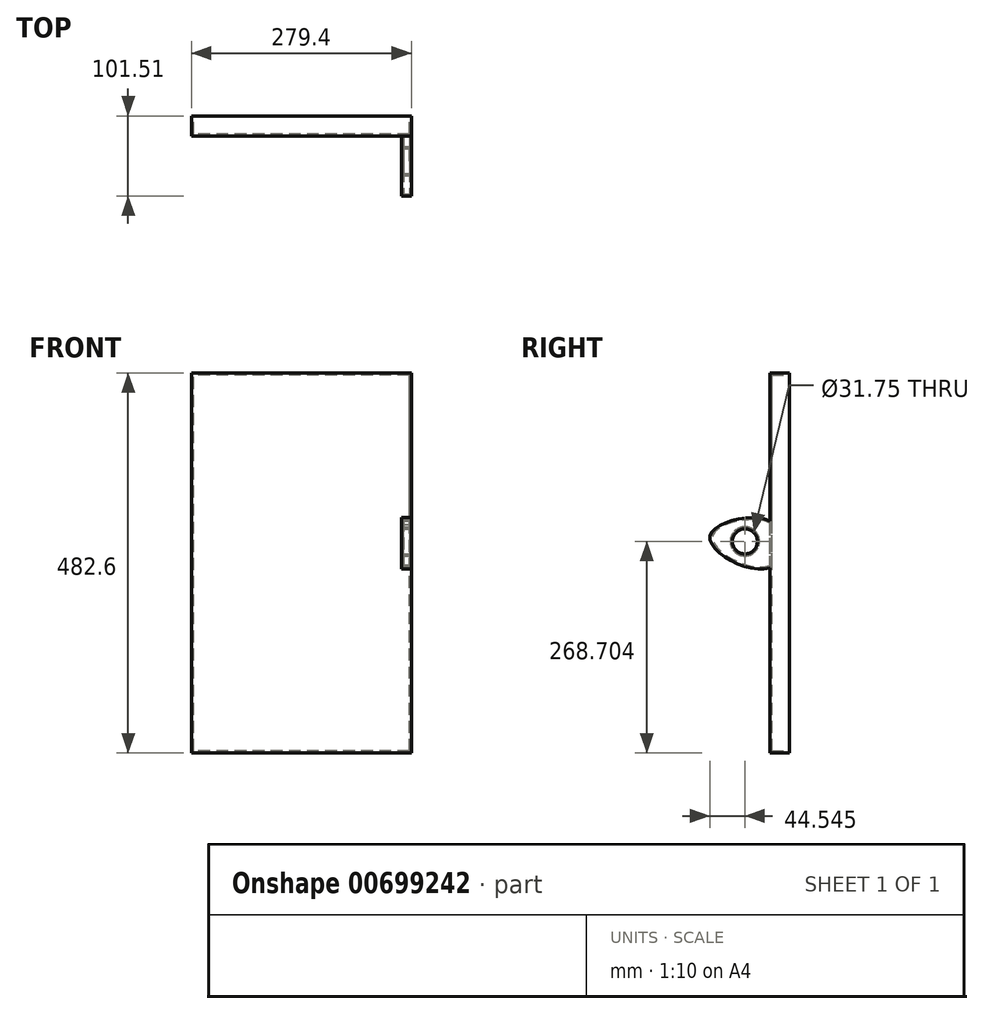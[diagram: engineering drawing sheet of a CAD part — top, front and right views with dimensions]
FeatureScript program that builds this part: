
annotation { "Feature Type Name" : "Feature", "Feature Type Description" : "" }
export const myFeature = defineFeature(function(context is Context, id is Id, definition is map)
    precondition{}
    {
        {
            var Q0;
            Q0=qCreatedBy(makeId("Front.planeOp"),FACE);
            var sketch = newSketch(context, id + "F0", { "sketchPlane" : qUnion([Q0])});
            skLineSegment(sketch, "E0.bottom", {"start": v(0, 0) * mm, "end": v(-279.4, 0) * mm});
            skLineSegment(sketch, "E0.top", {"start": v(0, 482.6) * mm, "end": v(-279.4, 482.6) * mm});
            skLineSegment(sketch, "E0.left", {"start": v(0, 0) * mm, "end": v(0, 482.6) * mm});
            skLineSegment(sketch, "E0.right", {"start": v(-279.4, 0) * mm, "end": v(-279.4, 482.6) * mm});
            skPoint(sketch, "E1.first.point", {"position": v(-64.83, 242.95) * mm});
            skPoint(sketch, "E1.second.point", {"position": v(-76.02, 242.95) * mm});
            skPoint(sketch, "E1.third.point", {"position": v(-52.5, 330.29) * mm});
            skSolve(sketch);
        }
        {
            var Q0;
            Q0=makeQuery(id+"F0.imprint","IMPRINT",FACE,{"disambiguationData":[TD([[makeQuery(id+"F0.imprint","IMPRINT",EDGE,{"derivedFrom":sQuery(id+"F0.wireOp",EDGE,"E0.bottom")}),-1.0]])]});
            extrude(context, id + "F1", {"entities" : qUnion([Q0]), "depth" : 25.4 * mm, "offsetDistance" : 25.4 * mm});
        }
        {
            var Q0;
            Q0=makeQuery(id+"F1.opExtrude","SWEPT_FACE",FACE,{"disambiguationData":[OSD([sQuery(id+"F0.wireOp",EDGE,"E0.left")])]});
            var sketch = newSketch(context, id + "F2", { "sketchPlane" : qUnion([Q0])});
            skPoint(sketch, "E2.0.internal.snap0", {"position": v(-25.4, 241.3) * mm});
            skPoint(sketch, "E2.4.internal.snap0", {"position": v(-25.4, 241.3) * mm});
            skFitSpline(sketch, "E2", {"points": [v(-15.12, 241.3) * mm, v(-14, 285.5) * mm, v(-61.03, 297.82) * mm, v(-101.34, 275.42) * mm, v(-68.86, 241.3) * mm, v(-15.12, 241.3) * mm]});
            skSolve(sketch);
        }
        {
            var Q0;
            {var subQ0=sQuery(id+"F2.wireOp",EDGE,"E2");var subQ1=makeQuery(id+"F1.opExtrude","CAP_EDGE",EDGE,{"disambiguationData":[OSD([sQuery(id+"F0.wireOp",EDGE,"E0.left")])],"isStart":false});var subQ2=makeQuery(id+"F2.imprint","INTERSECT",VERTEX,{"disambiguationData":[OD(0.0)],"derivedFrom":[subQ1,subQ0]});Q0=makeQuery(id+"F2.imprint","IMPRINT",FACE,{"disambiguationData":[TD([[makeQuery(id+"F2.imprint","IMPRINT",EDGE,{"disambiguationData":[TD([[subQ2,1.0]])],"derivedFrom":subQ0}),1.0]])]});}
            extrude(context, id + "F3", {"entities" : qUnion([Q0]), "operationType" : NewBodyOperationType.ADD, "oppositeDirection" : true, "depth" : 12.7 * mm, "offsetDistance" : 25.4 * mm});
        }
        {
            var Q0;
            {var subQ0=sQuery(id+"F0.wireOp",EDGE,"E0.left");Q0=makeQuery(id+"F3.boolean.opBoolean","MERGE",FACE,{"derivedFrom":[makeQuery(id+"F1.opExtrude","SWEPT_FACE",FACE,{"disambiguationData":[OSD([subQ0])]}),makeQuery(id+"F3.opExtrude","CAP_FACE",FACE,{"disambiguationData":[OSD([subQ0,sQuery(id+"F2.wireOp",EDGE,"E2")])],"isStart":true})]});}
            var sketch = newSketch(context, id + "F4", { "sketchPlane" : qUnion([Q0])});
            skCircle(sketch, "E3", {"center": v(-56.97, 268.7) * mm, "radius": 19.59 * mm});
            skSolve(sketch);
        }
        {
            var Q0;
            Q0=sQuery(id+"F4.wireOp",VERTEX,"E3.center");
            var Q1;
            Q1=makeQuery(id+"F1.opExtrude","SWEPT_BODY",BODY,{"disambiguationData":[OSD([sQuery(id+"F0.wireOp",EDGE,"E0.bottom"),sQuery(id+"F0.wireOp",EDGE,"E0.top"),sQuery(id+"F0.wireOp",EDGE,"E0.left"),sQuery(id+"F0.wireOp",EDGE,"E0.right")])]});
            hole(context, id + "F5", {"style" : HoleStyle.SIMPLE, "endStyle" : HoleEndStyle.THROUGH, "holeDiameter" : 31.75 * mm, "majorDiameter" : 6.35 * mm, "isTappedThrough" : true, "tappedDepth" : 12.7 * mm, "tapClearance" : 3, "locations" : qUnion([Q0]), "scope" : qUnion([Q1])});
        }
        {
            var Q0;
            Q0=makeQuery(id+"F1.opExtrude","CAP_FACE",FACE,{"disambiguationData":[OSD([sQuery(id+"F0.wireOp",EDGE,"E0.bottom"),sQuery(id+"F0.wireOp",EDGE,"E0.top"),sQuery(id+"F0.wireOp",EDGE,"E0.left"),sQuery(id+"F0.wireOp",EDGE,"E0.right")])],"isStart":true});
            shell(context, id + "F6", {"entities" : qUnion([Q0]), "thickness" : 2.54 * mm});
        }
    });
